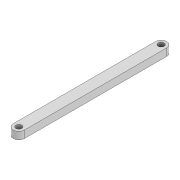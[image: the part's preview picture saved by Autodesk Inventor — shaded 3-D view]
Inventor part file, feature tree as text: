
AUTODESK INVENTOR PART (.ipt)
format: ipt  version: 2022 (Build 260153000, 153)  size: 85,504 bytes
history: native  units: mm
features: extrude x1, sketch x1
ambient origin geometry x8: Origin, YZ Plane, XZ Plane, XY Plane, X Axis, Y Axis, Z Axis, Center Point
bodies: Solid1 (feature_tree)
feature tree (2):
  extrude  "Extrusion1"  Depth=4.0mm
  sketch  "Sketch1"  dims[d0=3.2mm d1=3.2mm d2=6.0mm d3=76.957mm d6=4.0mm d7=0.0mm]
